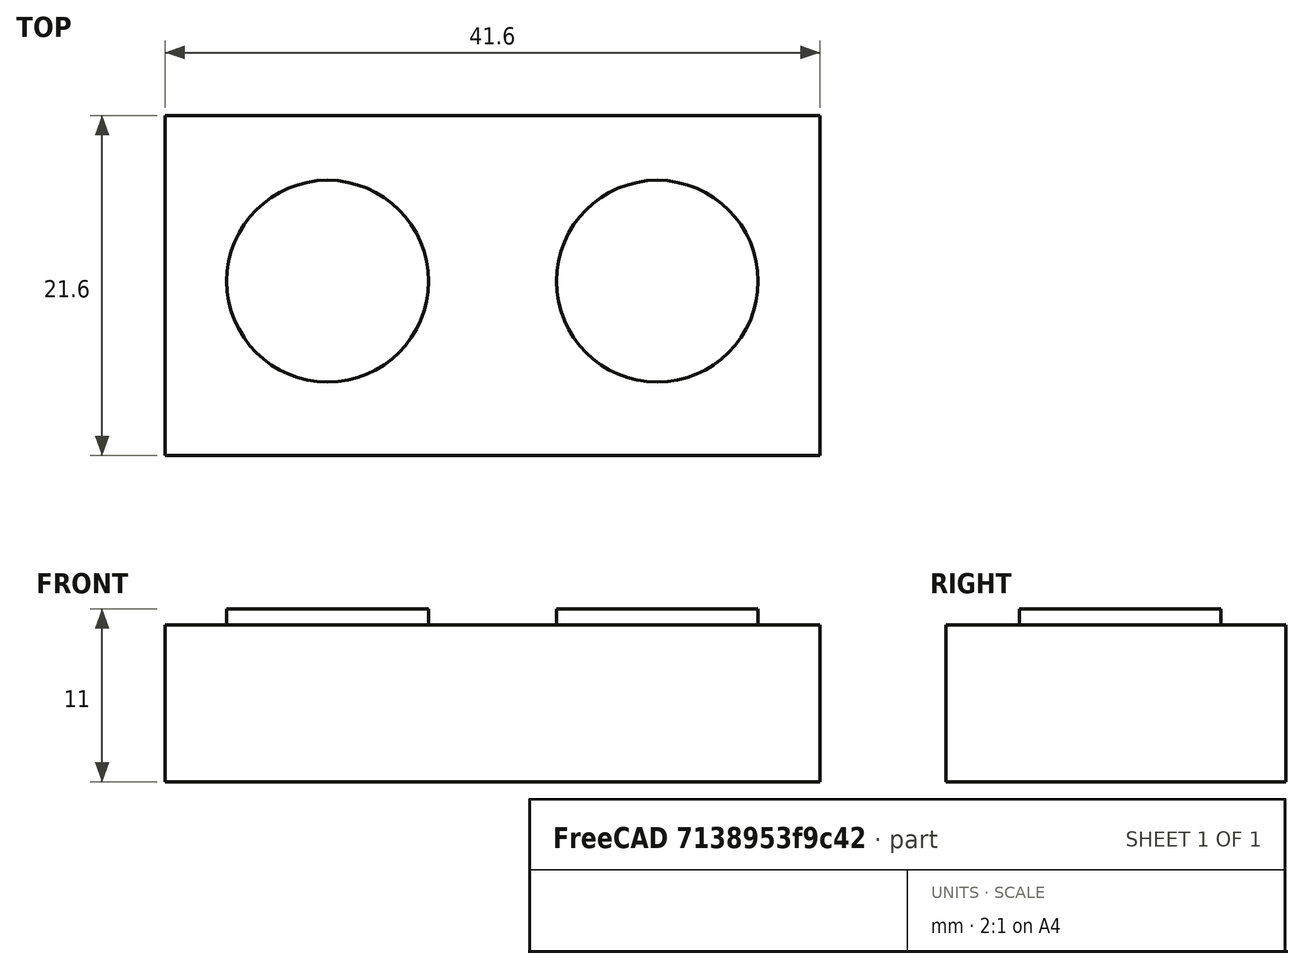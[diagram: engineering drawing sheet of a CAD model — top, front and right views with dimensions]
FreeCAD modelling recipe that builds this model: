
FCSTD DOCUMENT  (FreeCAD 0.18R14778 (Git))
Label: sketchexport_brocken
License: All rights reserved
LicenseURL: http://en.wikipedia.org/wiki/All_rights_reserved
objects: Sketcher::SketchExport×2, PartDesign::Pad×2, Sketcher::SketchObject×1, PartDesign::Body×1
note: 8 computed .brp shape members not serialized (recipe doc carries the construction recipe); baked Part::Feature solids carry a one-line shape summary decoded from their .brp

FEATURE [Sketcher::SketchExport] Export
  Base = Sketch
  Refs = ;g1;SKT.Edge1 | ;g2;SKT.Edge2 | ;g3;SKT.Edge3 | ;g4;SKT.Edge4
  SyncPlacement = true
FEATURE [PartDesign::Pad] Pad
  ClaimChildren = false
  Length = 10
  Length2 = 100
  Profile = -> Export
  Type = 0
FEATURE [Sketcher::SketchExport] Export001
  Base = Sketch
  MapMode = 5
  Placement = pos=(0,0,10) rot=(0,0,1;0rad)
  Refs = ;g13;SKT.Edge5 | ;g14;SKT.Edge6
  Support = -> [Pad]
  SyncPlacement = true
FEATURE [Sketcher::SketchObject] Sketch
  Exports = -> [Export,Export001]
  LastGeoID = 14
  MapMode = 5
  Support = -> [XY_Plane]
  sketch-geometry (6):
    g0: LineSegment StartX=-20.7982 StartY=4.60942 StartZ=0 EndX=20.7982 EndY=4.60942 EndZ=0
    g1: LineSegment StartX=20.7982 StartY=4.60942 StartZ=0 EndX=20.7982 EndY=-4.99141 EndZ=0
    g2: LineSegment StartX=20.7982 StartY=-4.99141 StartZ=0 EndX=-20.7982 EndY=-4.99141 EndZ=0
    g3: LineSegment StartX=-20.7982 StartY=-4.99141 StartZ=0 EndX=-20.7982 EndY=4.60942 EndZ=0
    g4: Circle CenterX=-10.4687 CenterY=0 CenterZ=0 NormalX=0 NormalY=0 NormalZ=1 AngleXU=0 Radius=2.65342
    g5: Circle CenterX=10.4687 CenterY=0 CenterZ=0 NormalX=0 NormalY=0 NormalZ=1 AngleXU=0 Radius=2.65342
  constraints (11):
    c: Coincident(g0,g1)
    c: Coincident(g1,g2)
    c: Coincident(g2,g3)
    c: Coincident(g3,g0)
    c: Horizontal(g0)
    c: Vertical(g1)
    c: Vertical(g3)
    c: PointOnObject(g5,g-1)
    c: Symmetric(g4,g5,g-2)
    c: Symmetric(g2,g1,g-2)
    c: Equal(g5,g4)
FEATURE [PartDesign::Pad] Pad001
  BaseFeature = -> Pad
  ClaimChildren = false
  Length = 1
  Length2 = 100
  Profile = -> Export001
  Type = 0
FEATURE [PartDesign::Body] Body
  Group = -> [Sketch,Export,Export001,Pad,Pad001]
  Origin = -> Origin
  Tip = -> Pad001
